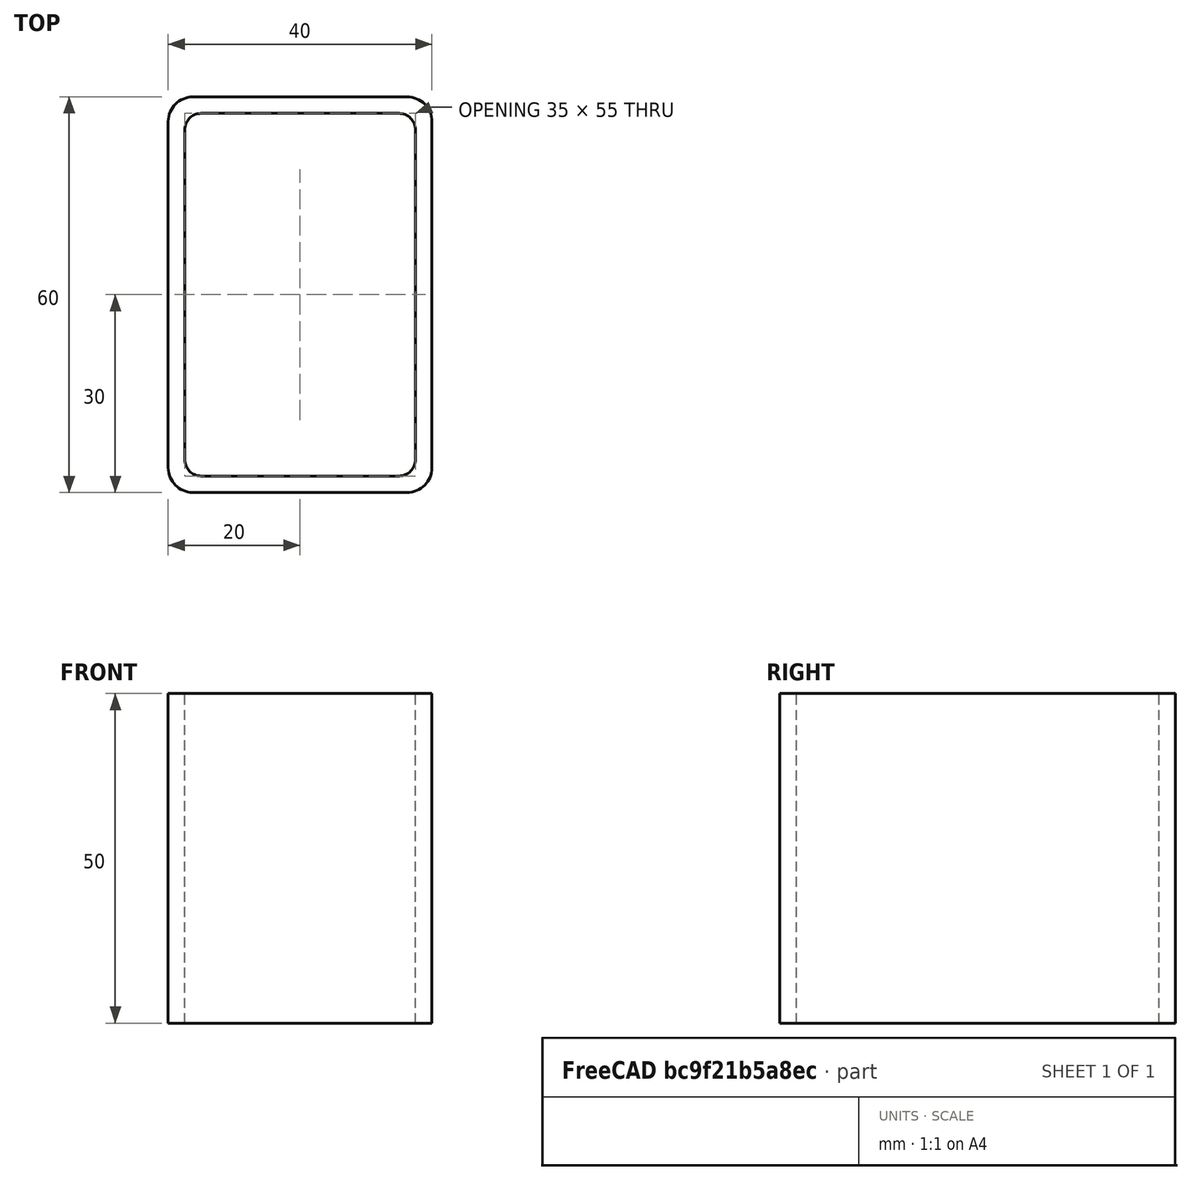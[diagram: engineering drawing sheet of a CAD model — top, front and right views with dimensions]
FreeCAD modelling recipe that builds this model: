
FCSTD DOCUMENT  (FreeCAD 0.15R4671 (Git))
Label: Rectangular hollow section 60x40x2.5 EN10219 S235JRH
License: All rights reserved
LicenseURL: http://en.wikipedia.org/wiki/All_rights_reserved
objects: Sketcher::SketchObject×1, Part::Extrusion×1
note: 2 computed .brp shape members not serialized (recipe doc carries the construction recipe); baked Part::Feature solids carry a one-line shape summary decoded from their .brp

FEATURE [Sketcher::SketchObject] Sketch
  sketch-geometry (16):
    g0: LineSegment StartX=-15 StartY=27.5 StartZ=0 EndX=15 EndY=27.5 EndZ=0
    g1: LineSegment StartX=17.5 StartY=25 StartZ=0 EndX=17.5 EndY=-25 EndZ=0
    g2: LineSegment StartX=15 StartY=-27.5 StartZ=0 EndX=-15 EndY=-27.5 EndZ=0
    g3: LineSegment StartX=-17.5 StartY=-25 StartZ=0 EndX=-17.5 EndY=25 EndZ=0
    g4: LineSegment StartX=-16.25 StartY=30 StartZ=0 EndX=16.25 EndY=30 EndZ=0
    g5: LineSegment StartX=20 StartY=26.25 StartZ=0 EndX=20 EndY=-26.25 EndZ=0
    g6: LineSegment StartX=16.25 StartY=-30 StartZ=0 EndX=-16.25 EndY=-30 EndZ=0
    g7: LineSegment StartX=-20 StartY=-26.25 StartZ=0 EndX=-20 EndY=26.25 EndZ=0
    g8: ArcOfCircle CenterX=-15 CenterY=25 CenterZ=0 NormalX=0 NormalY=0 NormalZ=1 Radius=2.5 StartAngle=1.5708 EndAngle=3.14159
    g9: ArcOfCircle CenterX=15 CenterY=25 CenterZ=0 NormalX=0 NormalY=0 NormalZ=1 Radius=2.5 StartAngle=0 EndAngle=1.5708
    g10: ArcOfCircle CenterX=15 CenterY=-25 CenterZ=0 NormalX=0 NormalY=0 NormalZ=1 Radius=2.5 StartAngle=4.71239 EndAngle=6.28319
    g11: ArcOfCircle CenterX=-15 CenterY=-25 CenterZ=0 NormalX=0 NormalY=0 NormalZ=1 Radius=2.5 StartAngle=3.14159 EndAngle=4.71239
    g12: ArcOfCircle CenterX=16.25 CenterY=26.25 CenterZ=0 NormalX=0 NormalY=0 NormalZ=1 Radius=3.75 StartAngle=0 EndAngle=1.5708
    g13: ArcOfCircle CenterX=16.25 CenterY=-26.25 CenterZ=0 NormalX=0 NormalY=0 NormalZ=1 Radius=3.75 StartAngle=4.71239 EndAngle=6.28319
    g14: ArcOfCircle CenterX=-16.25 CenterY=-26.25 CenterZ=0 NormalX=0 NormalY=0 NormalZ=1 Radius=3.75 StartAngle=3.14159 EndAngle=4.71239
    g15: ArcOfCircle CenterX=-16.25 CenterY=26.25 CenterZ=0 NormalX=0 NormalY=0 NormalZ=1 Radius=3.75 StartAngle=1.5708 EndAngle=3.14159
  constraints (36):
    c: Horizontal(g2)
    c: Vertical(g3)
    c: Horizontal(g6)
    c: Vertical(g7)
    c: Tangent(g3,g8) = 1.5708
    c: Tangent(g0,g8) = 1.5708
    c: Tangent(g0,g9) = 1.5708
    c: Tangent(g1,g9) = 1.5708
    c: Tangent(g1,g10) = 1.5708
    c: Tangent(g2,g10) = 1.5708
    c: Tangent(g2,g11) = 1.5708
    c: Tangent(g3,g11) = 1.5708
    c: Tangent(g4,g12) = 1.5708
    c: Tangent(g5,g12) = 1.5708
    c: Tangent(g5,g13) = 1.5708
    c: Tangent(g6,g13) = 1.5708
    c: Tangent(g6,g14) = 1.5708
    c: Tangent(g7,g14) = 1.5708
    c: Tangent(g7,g15) = 1.5708
    c: Tangent(g4,g15) = 1.5708
    c: Equal(g9,g8)
    c: Equal(g9,g11)
    c: Equal(g9,g10)
    c: Equal(g12,g15)
    c: Equal(g12,g14)
    c: Equal(g12,g13)
    c: Symmetric(g4,g6,g-1)
    c: Symmetric(g7,g5,g-2)
    c: DistanceY(g4,g6) = -60
    c: DistanceX(g7,g5) = 40
    c: Symmetric(g3,g1,g-2)
    c: Symmetric(g0,g2,g-1)
    c: DistanceY(g0,g4) = 2.5
    c: DistanceX(g5,g1) = -2.5
    c: Radius(g9) = 2.5
    c: Radius(g12) = 3.75
FEATURE [Part::Extrusion] Extrude  label="Rectangular hollow section 60x40x2.5 EN10219 S235JRH"
  Base = -> Sketch
  Dir = (0,0,50)
  Solid = true
